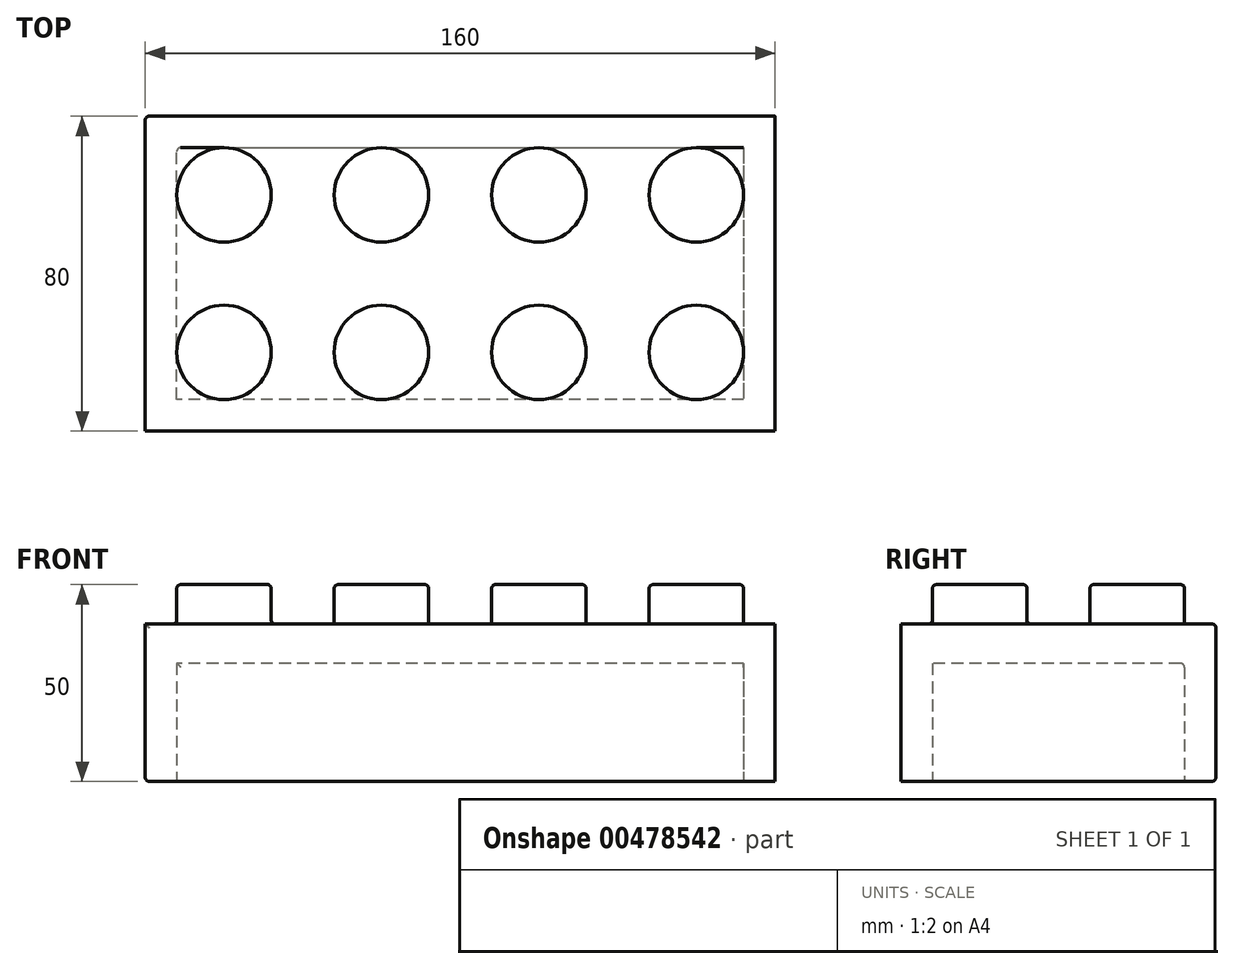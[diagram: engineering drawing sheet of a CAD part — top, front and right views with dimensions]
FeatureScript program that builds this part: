
annotation { "Feature Type Name" : "Feature", "Feature Type Description" : "" }
export const myFeature = defineFeature(function(context is Context, id is Id, definition is map)
    precondition{}
    {
        {
            var Q0;
            Q0=qCreatedBy(makeId("Top.planeOp"),FACE);
            var sketch = newSketch(context, id + "F0", { "sketchPlane" : qUnion([Q0])});
            skLineSegment(sketch, "E0.bottom", {"start": v(80, 40) * mm, "end": v(-80, 40) * mm});
            skLineSegment(sketch, "E0.top", {"start": v(80, -40) * mm, "end": v(-80, -40) * mm});
            skLineSegment(sketch, "E0.left", {"start": v(80, 40) * mm, "end": v(80, -40) * mm});
            skLineSegment(sketch, "E0.right", {"start": v(-80, 40) * mm, "end": v(-80, -40) * mm});
            skPoint(sketch, "E0.middle", {"position": v(0, 0) * mm});
            skSolve(sketch);
        }
        {
            var Q0;
            Q0 = qSketchRegion(id + "F0", true);
            extrude(context, id + "F1", {"entities" : qUnion([Q0]), "depth" : 40 * mm});
        }
        {
            var Q0;
            Q0=makeQuery(id+"F1.opExtrude","CAP_FACE",FACE,{"disambiguationData":[OSD([sQuery(id+"F0.wireOp",EDGE,"E0.bottom"),sQuery(id+"F0.wireOp",EDGE,"E0.top"),sQuery(id+"F0.wireOp",EDGE,"E0.left"),sQuery(id+"F0.wireOp",EDGE,"E0.right")])],"isStart":true});
            var sketch = newSketch(context, id + "F2", { "sketchPlane" : qUnion([Q0])});
            skLineSegment(sketch, "E1.0", {"start": v(72, 32) * mm, "end": v(-72, 32) * mm});
            skLineSegment(sketch, "E1.1", {"start": v(72, -32) * mm, "end": v(72, 32) * mm});
            skLineSegment(sketch, "E1.2", {"start": v(-72, -32) * mm, "end": v(72, -32) * mm});
            skLineSegment(sketch, "E1.3", {"start": v(-72, 32) * mm, "end": v(-72, -32) * mm});
            skSolve(sketch);
        }
        {
            var Q0;
            Q0 = qSketchRegion(id + "F2", true);
            extrude(context, id + "F3", {"entities" : qUnion([Q0]), "operationType" : NewBodyOperationType.REMOVE, "oppositeDirection" : true, "depth" : 30 * mm});
        }
        {
            var Q0;
            Q0=makeQuery(id+"F1.opExtrude","CAP_FACE",FACE,{"disambiguationData":[OSD([sQuery(id+"F0.wireOp",EDGE,"E0.bottom"),sQuery(id+"F0.wireOp",EDGE,"E0.top"),sQuery(id+"F0.wireOp",EDGE,"E0.left"),sQuery(id+"F0.wireOp",EDGE,"E0.right")])],"isStart":false});
            var sketch = newSketch(context, id + "F4", { "sketchPlane" : qUnion([Q0])});
            skCircle(sketch, "E2", {"center": v(-60, 20) * mm, "radius": 12 * mm});
            skCircle(sketch, "E3.0.1.0", {"center": v(-60, -20) * mm, "radius": 12 * mm});
            skCircle(sketch, "E3.1.0.0", {"center": v(-20, 20) * mm, "radius": 12 * mm});
            skCircle(sketch, "E3.1.1.0", {"center": v(-20, -20) * mm, "radius": 12 * mm});
            skCircle(sketch, "E3.2.0.0", {"center": v(20, 20) * mm, "radius": 12 * mm});
            skCircle(sketch, "E3.2.1.0", {"center": v(20, -20) * mm, "radius": 12 * mm});
            skCircle(sketch, "E3.3.0.0", {"center": v(60, 20) * mm, "radius": 12 * mm});
            skCircle(sketch, "E3.3.1.0", {"center": v(60, -20) * mm, "radius": 12 * mm});
            skLineSegment(sketch, "E3.direction1", {"start": v(-60, 20) * mm, "end": v(-20, 20) * mm, "construction": true});
            skLineSegment(sketch, "E3.direction2", {"start": v(-60, 20) * mm, "end": v(-60, -20) * mm, "construction": true});
            skSolve(sketch);
        }
        {
            var Q0;
            Q0 = qSketchRegion(id + "F4", true);
            extrude(context, id + "F5", {"entities" : qUnion([Q0]), "operationType" : NewBodyOperationType.ADD, "depth" : 10 * mm});
        }
        {
            var Q0;
            Q0=makeQuery(id+"F5.opExtrude","CAP_FACE",FACE,{"disambiguationData":[OSD([sQuery(id+"F4.wireOp",EDGE,"E2")])],"isStart":false});
            fillet(context, id + "F6", {"entities" : qUnion([Q0]), "radius" : 1 * mm, "tangentPropagation" : true, "allowEdgeOverflow" : false});
        }
        {
            var Q0;
            Q0=makeQuery(id+"F5.opExtrude","CAP_FACE",FACE,{"disambiguationData":[OSD([sQuery(id+"F4.wireOp",EDGE,"E3.1.0.0")])],"isStart":false});
            fillet(context, id + "F7", {"entities" : qUnion([Q0]), "radius" : 1 * mm, "tangentPropagation" : true, "allowEdgeOverflow" : false});
        }
        {
            var Q0;
            Q0=makeQuery(id+"F5.opExtrude","CAP_FACE",FACE,{"disambiguationData":[OSD([sQuery(id+"F4.wireOp",EDGE,"E3.2.0.0")])],"isStart":false});
            var Q1;
            Q1=makeQuery(id+"F5.opExtrude","CAP_FACE",FACE,{"disambiguationData":[OSD([sQuery(id+"F4.wireOp",EDGE,"E3.3.0.0")])],"isStart":false});
            fillet(context, id + "F8", {"entities" : qUnion([Q0, Q1]), "radius" : 1 * mm, "tangentPropagation" : true, "allowEdgeOverflow" : false});
        }
        {
            var Q0;
            Q0=makeQuery(id+"F5.opExtrude","SWEPT_FACE",FACE,{"disambiguationData":[OSD([sQuery(id+"F4.wireOp",EDGE,"E3.0.1.0")])]});
            var Q1;
            Q1=makeQuery(id+"F5.opExtrude","CAP_FACE",FACE,{"disambiguationData":[OSD([sQuery(id+"F4.wireOp",EDGE,"E3.1.1.0")])],"isStart":false});
            var Q2;
            Q2=makeQuery(id+"F5.opExtrude","CAP_FACE",FACE,{"disambiguationData":[OSD([sQuery(id+"F4.wireOp",EDGE,"E3.2.1.0")])],"isStart":false});
            var Q3;
            Q3=makeQuery(id+"F5.opExtrude","CAP_FACE",FACE,{"disambiguationData":[OSD([sQuery(id+"F4.wireOp",EDGE,"E3.3.1.0")])],"isStart":false});
            var Q4;
            Q4=makeQuery(id+"F1.opExtrude","SWEPT_EDGE",EDGE,{"disambiguationData":[OSD([sQuery(id+"F0.wireOp",EDGE,"E0.bottom"),sQuery(id+"F0.wireOp",EDGE,"E0.right")])]});
            var Q5;
            Q5=makeQuery(id+"F1.opExtrude","CAP_EDGE",EDGE,{"disambiguationData":[OSD([sQuery(id+"F0.wireOp",EDGE,"E0.bottom")])],"isStart":true});
            var Q6;
            Q6=makeQuery(id+"F1.opExtrude","CAP_EDGE",EDGE,{"disambiguationData":[OSD([sQuery(id+"F0.wireOp",EDGE,"E0.bottom")])],"isStart":false});
            var Q7;
            Q7=makeQuery(id+"F1.opExtrude","CAP_EDGE",EDGE,{"disambiguationData":[OSD([sQuery(id+"F0.wireOp",EDGE,"E0.right")])],"isStart":true});
            var Q8;
            Q8=makeQuery(id+"F3.boolean.opBoolean","COPY",EDGE,{"derivedFrom":makeQuery(id+"F3.opExtrude","SWEPT_EDGE",EDGE,{"disambiguationData":[OSD([sQuery(id+"F2.wireOp",EDGE,"E1.2"),sQuery(id+"F2.wireOp",EDGE,"E1.3")])]})});
            var Q9;
            Q9=makeQuery(id+"F3.boolean.opBoolean","COPY",EDGE,{"derivedFrom":makeQuery(id+"F3.opExtrude","CAP_EDGE",EDGE,{"disambiguationData":[OSD([sQuery(id+"F2.wireOp",EDGE,"E1.2")])],"isStart":false})});
            fillet(context, id + "F9", {"entities" : qUnion([Q0, Q1, Q2, Q3, Q4, Q5, Q6, Q7, Q8, Q9]), "radius" : 1 * mm, "tangentPropagation" : true, "allowEdgeOverflow" : false});
        }
    });
